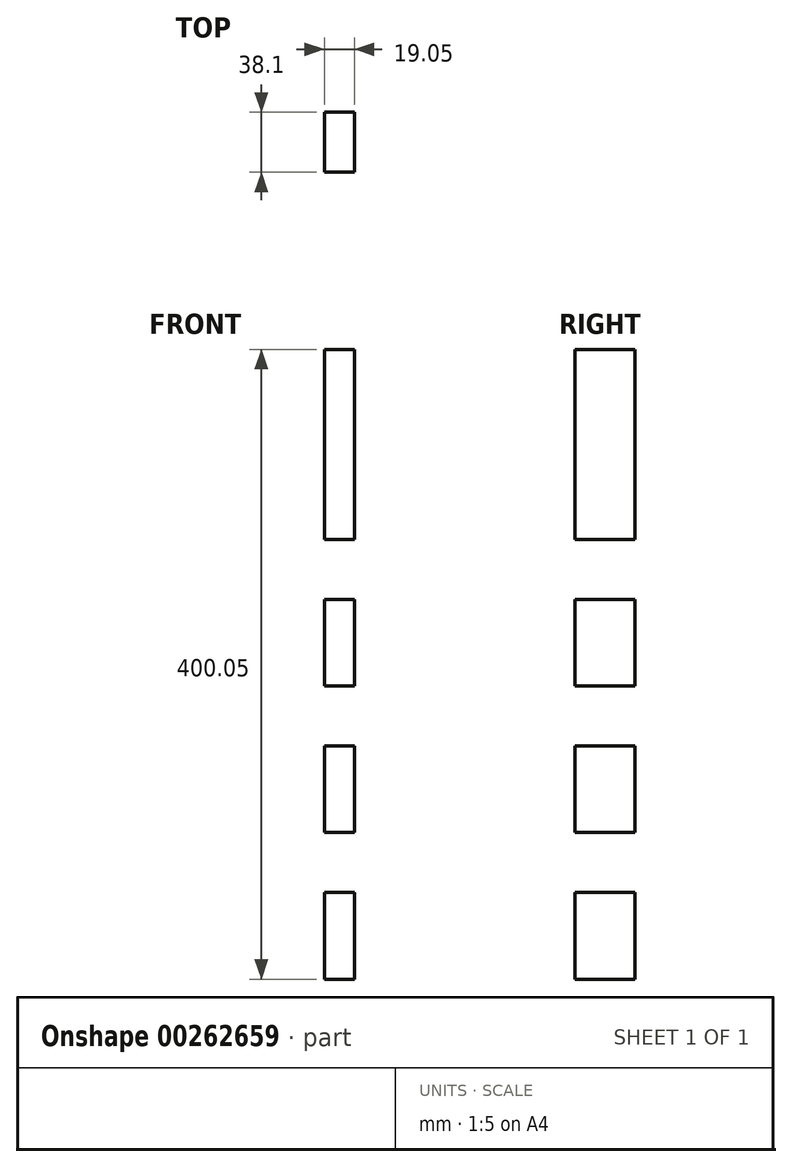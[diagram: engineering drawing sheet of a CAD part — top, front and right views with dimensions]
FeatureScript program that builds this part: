
annotation { "Feature Type Name" : "Feature", "Feature Type Description" : "" }
export const myFeature = defineFeature(function(context is Context, id is Id, definition is map)
    precondition{}
    {
        {
            var Q0;
            Q0=qCreatedBy(makeId("Front.planeOp"),FACE);
            var sketch = newSketch(context, id + "F0", { "sketchPlane" : qUnion([Q0])});
            skLineSegment(sketch, "E0", {"start": v(0, 0) * mm, "end": v(0, -457.2) * mm});
            skLineSegment(sketch, "E1", {"start": v(0, 0) * mm, "end": v(-9.52, 0) * mm});
            skLineSegment(sketch, "E2", {"start": v(-9.52, 0) * mm, "end": v(-9.52, -38.1) * mm});
            skLineSegment(sketch, "E3", {"start": v(0, -38.1) * mm, "end": v(-19.05, -38.1) * mm});
            skLineSegment(sketch, "E4", {"start": v(-19.05, -38.1) * mm, "end": v(-19.05, -158.72) * mm});
            skLineSegment(sketch, "E5", {"start": v(-19.05, -158.72) * mm, "end": v(0, -158.72) * mm});
            skLineSegment(sketch, "E6", {"start": v(-9.52, -158.72) * mm, "end": v(-9.52, -196.82) * mm});
            skLineSegment(sketch, "E7", {"start": v(0, -196.82) * mm, "end": v(-19.05, -196.82) * mm});
            skLineSegment(sketch, "E8", {"start": v(-19.05, -196.82) * mm, "end": v(-19.05, -251.87) * mm});
            skLineSegment(sketch, "E9", {"start": v(-19.05, -251.87) * mm, "end": v(0, -251.87) * mm});
            skLineSegment(sketch, "E10", {"start": v(-9.52, -251.87) * mm, "end": v(-9.52, -289.97) * mm});
            skLineSegment(sketch, "E11", {"start": v(0, -289.97) * mm, "end": v(-19.05, -289.97) * mm});
            skLineSegment(sketch, "E12", {"start": v(-19.05, -289.97) * mm, "end": v(-19.05, -345) * mm});
            skLineSegment(sketch, "E13", {"start": v(-19.05, -345) * mm, "end": v(0, -345) * mm});
            skLineSegment(sketch, "E14", {"start": v(-9.52, -345) * mm, "end": v(-9.52, -383.1) * mm});
            skLineSegment(sketch, "E15", {"start": v(0, -383.1) * mm, "end": v(-19.05, -383.1) * mm});
            skLineSegment(sketch, "E16", {"start": v(-19.05, -383.1) * mm, "end": v(-19.05, -438.15) * mm});
            skLineSegment(sketch, "E17", {"start": v(-19.05, -438.15) * mm, "end": v(0, -438.15) * mm});
            skLineSegment(sketch, "E18", {"start": v(-9.52, -438.15) * mm, "end": v(-9.52, -457.2) * mm});
            skLineSegment(sketch, "E19", {"start": v(-9.52, -457.2) * mm, "end": v(0, -457.2) * mm});
            skSolve(sketch);
        }
        {
            var Q0;
            {var subQ0=sQuery(id+"F0.wireOp",EDGE,"E4");Q0=makeQuery(id+"F0.imprint","IMPRINT",FACE,{"disambiguationData":[TD([[makeQuery(id+"F0.imprint","IMPRINT",EDGE,{"derivedFrom":subQ0}),1.0]])]});}
            var Q1;
            {var subQ0=sQuery(id+"F0.wireOp",EDGE,"E8");Q1=makeQuery(id+"F0.imprint","IMPRINT",FACE,{"disambiguationData":[TD([[makeQuery(id+"F0.imprint","IMPRINT",EDGE,{"derivedFrom":subQ0}),1.0]])]});}
            var Q2;
            {var subQ2=sQuery(id+"F0.wireOp",EDGE,"E12");Q2=makeQuery(id+"F0.imprint","IMPRINT",FACE,{"disambiguationData":[TD([[makeQuery(id+"F0.imprint","IMPRINT",EDGE,{"derivedFrom":subQ2}),1.0]])]});}
            var Q3;
            {var subQ0=sQuery(id+"F0.wireOp",EDGE,"E16");Q3=makeQuery(id+"F0.imprint","IMPRINT",FACE,{"disambiguationData":[TD([[makeQuery(id+"F0.imprint","IMPRINT",EDGE,{"derivedFrom":subQ0}),1.0]])]});}
            extrude(context, id + "F1", {"entities" : qUnion([Q0, Q1, Q2, Q3]), "offsetDistance" : 25.4 * mm, "depth" : 38.1 * mm});
        }
    });
